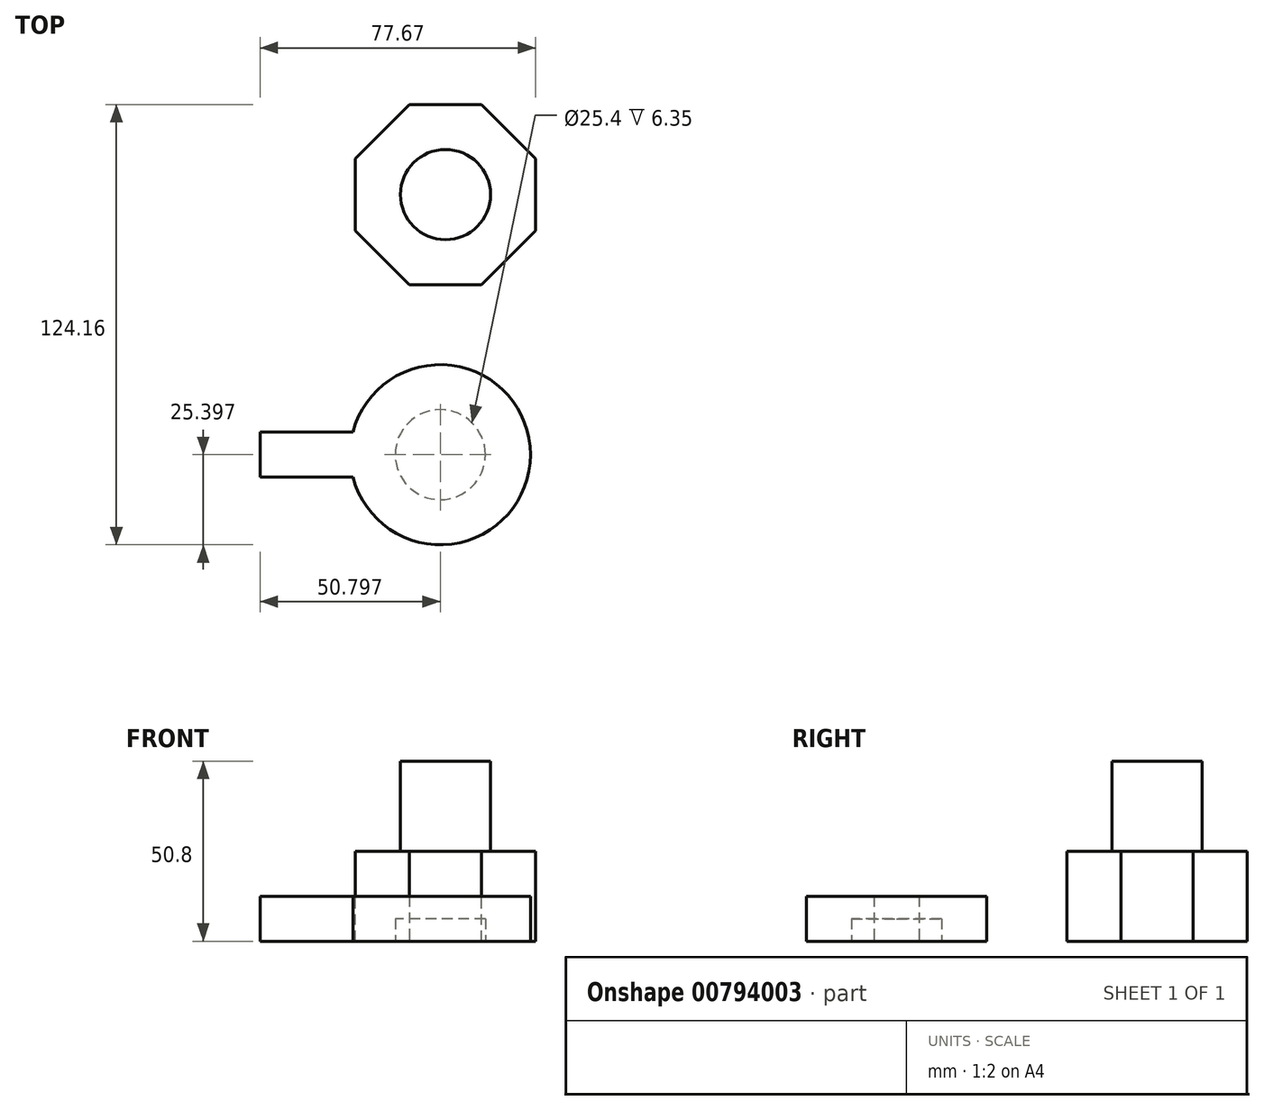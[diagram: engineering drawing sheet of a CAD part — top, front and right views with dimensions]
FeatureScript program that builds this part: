
annotation { "Feature Type Name" : "Feature", "Feature Type Description" : "" }
export const myFeature = defineFeature(function(context is Context, id is Id, definition is map)
    precondition{}
    {
        {
            var Q0;
            Q0=qCreatedBy(makeId("Top.planeOp"),FACE);
            var sketch = newSketch(context, id + "F0", { "sketchPlane" : qUnion([Q0])});
            skLineSegment(sketch, "E0.bottom", {"start": v(-25.4, 25.4) * mm, "end": v(25.4, 25.4) * mm});
            skLineSegment(sketch, "E0.top", {"start": v(-25.4, -25.4) * mm, "end": v(25.4, -25.4) * mm});
            skLineSegment(sketch, "E0.left", {"start": v(-25.4, 25.4) * mm, "end": v(-25.4, -25.4) * mm});
            skLineSegment(sketch, "E0.right", {"start": v(25.4, 25.4) * mm, "end": v(25.4, -25.4) * mm});
            skPoint(sketch, "E0.middle", {"position": v(0, 0) * mm});
            skCircle(sketch, "E1", {"center": v(0, 0) * mm, "radius": 12.7 * mm});
            skSolve(sketch);
        }
        {
            var Q0;
            Q0=makeQuery(id+"F0.imprint","IMPRINT",FACE,{"disambiguationData":[TD([[makeQuery(id+"F0.imprint","IMPRINT",EDGE,{"derivedFrom":sQuery(id+"F0.wireOp",EDGE,"E1")}),1.0]])]});
            var Q1;
            Q1=makeQuery(id+"F0.imprint","IMPRINT",FACE,{"disambiguationData":[TD([[makeQuery(id+"F0.imprint","IMPRINT",EDGE,{"derivedFrom":sQuery(id+"F0.wireOp",EDGE,"E0.bottom")}),-1.0]])]});
            extrude(context, id + "F1", {"entities" : qUnion([Q0, Q1]), "depth" : 25.4 * mm, "offsetDistance" : 25.4 * mm});
        }
        {
            var Q0;
            Q0=makeQuery(id+"F0.imprint","IMPRINT",FACE,{"disambiguationData":[TD([[makeQuery(id+"F0.imprint","IMPRINT",EDGE,{"derivedFrom":sQuery(id+"F0.wireOp",EDGE,"E1")}),1.0]])]});
            extrude(context, id + "F2", {"entities" : qUnion([Q0]), "operationType" : NewBodyOperationType.ADD, "depth" : 50.8 * mm, "offsetDistance" : 25.4 * mm});
        }
        {
            var Q0;
            Q0=makeQuery(id+"F1.opExtrude","SWEPT_EDGE",EDGE,{"disambiguationData":[OSD([sQuery(id+"F0.wireOp",EDGE,"E0.top"),sQuery(id+"F0.wireOp",EDGE,"E0.left")])]});
            var Q1;
            Q1=makeQuery(id+"F1.opExtrude","SWEPT_EDGE",EDGE,{"disambiguationData":[OSD([sQuery(id+"F0.wireOp",EDGE,"E0.top"),sQuery(id+"F0.wireOp",EDGE,"E0.right")])]});
            var Q2;
            Q2=makeQuery(id+"F1.opExtrude","SWEPT_EDGE",EDGE,{"disambiguationData":[OSD([sQuery(id+"F0.wireOp",EDGE,"E0.bottom"),sQuery(id+"F0.wireOp",EDGE,"E0.right")])]});
            var Q3;
            Q3=makeQuery(id+"F1.opExtrude","SWEPT_EDGE",EDGE,{"disambiguationData":[OSD([sQuery(id+"F0.wireOp",EDGE,"E0.bottom"),sQuery(id+"F0.wireOp",EDGE,"E0.left")])]});
            chamfer(context, id + "F3", {"entities" : qUnion([Q0, Q1, Q2, Q3]), "width" : 15.24 * mm, "tangentPropagation" : true});
        }
        {
            var Q0;
            Q0=qCreatedBy(makeId("Top.planeOp"),FACE);
            var sketch = newSketch(context, id + "F4", { "sketchPlane" : qUnion([Q0])});
            skCircle(sketch, "E2", {"center": v(-1.47, -73.36) * mm, "radius": 25.4 * mm});
            skLineSegment(sketch, "E3.bottom", {"start": v(-1.47, -67.01) * mm, "end": v(-52.27, -67.01) * mm});
            skLineSegment(sketch, "E3.top", {"start": v(-1.47, -79.71) * mm, "end": v(-52.27, -79.71) * mm});
            skLineSegment(sketch, "E3.left", {"start": v(-1.47, -67.01) * mm, "end": v(-1.47, -79.71) * mm});
            skLineSegment(sketch, "E3.right", {"start": v(-52.27, -67.01) * mm, "end": v(-52.27, -79.71) * mm});
            skCircle(sketch, "E4", {"center": v(-1.47, -73.36) * mm, "radius": 12.7 * mm});
            skSolve(sketch);
        }
        {
            var Q0;
            {var subQ5=sQuery(id+"F4.wireOp",EDGE,"E3.right");Q0=makeQuery(id+"F4.imprint","IMPRINT",FACE,{"disambiguationData":[TD([[makeQuery(id+"F4.imprint","IMPRINT",EDGE,{"derivedFrom":subQ5}),1.0]])]});}
            var Q1;
            {var subQ0=sQuery(id+"F4.wireOp",EDGE,"E3.bottom");var subQ1=sQuery(id+"F4.wireOp",EDGE,"E2");var subQ2=makeQuery(id+"F4.imprint","INTERSECT",VERTEX,{"derivedFrom":[subQ1,subQ0]});Q1=makeQuery(id+"F4.imprint","IMPRINT",FACE,{"disambiguationData":[TD([[makeQuery(id+"F4.imprint","IMPRINT",EDGE,{"disambiguationData":[TD([[subQ2,1.0]])],"derivedFrom":subQ1}),1.0]])]});}
            var Q2;
            {var subQ0=sQuery(id+"F4.wireOp",EDGE,"E3.bottom");var subQ1=sQuery(id+"F4.wireOp",EDGE,"E2");var subQ2=makeQuery(id+"F4.imprint","INTERSECT",VERTEX,{"derivedFrom":[subQ1,subQ0]});Q2=makeQuery(id+"F4.imprint","IMPRINT",FACE,{"disambiguationData":[TD([[makeQuery(id+"F4.imprint","IMPRINT",EDGE,{"disambiguationData":[TD([[subQ2,-1.0]])],"derivedFrom":subQ1}),1.0]])]});}
            var Q3;
            {var subQ0=sQuery(id+"F4.wireOp",EDGE,"E3.left");Q3=makeQuery(id+"F4.imprint","IMPRINT",FACE,{"disambiguationData":[TD([[makeQuery(id+"F4.imprint","IMPRINT",EDGE,{"derivedFrom":subQ0}),-1.0]])]});}
            var Q4;
            {var subQ0=sQuery(id+"F4.wireOp",EDGE,"E3.left");Q4=makeQuery(id+"F4.imprint","IMPRINT",FACE,{"disambiguationData":[TD([[makeQuery(id+"F4.imprint","IMPRINT",EDGE,{"derivedFrom":subQ0}),1.0]])]});}
            extrude(context, id + "F5", {"entities" : qUnion([Q0, Q1, Q2, Q3, Q4]), "depth" : 12.7 * mm, "offsetDistance" : 25.4 * mm});
        }
        {
            var Q0;
            {var subQ0=sQuery(id+"F4.wireOp",EDGE,"E3.left");Q0=makeQuery(id+"F4.imprint","IMPRINT",FACE,{"disambiguationData":[TD([[makeQuery(id+"F4.imprint","IMPRINT",EDGE,{"derivedFrom":subQ0}),1.0]])]});}
            var Q1;
            {var subQ0=sQuery(id+"F4.wireOp",EDGE,"E3.left");Q1=makeQuery(id+"F4.imprint","IMPRINT",FACE,{"disambiguationData":[TD([[makeQuery(id+"F4.imprint","IMPRINT",EDGE,{"derivedFrom":subQ0}),-1.0]])]});}
            extrude(context, id + "F6", {"entities" : qUnion([Q0, Q1]), "operationType" : NewBodyOperationType.REMOVE, "depth" : 6.35 * mm, "offsetDistance" : 25.4 * mm});
        }
    });
